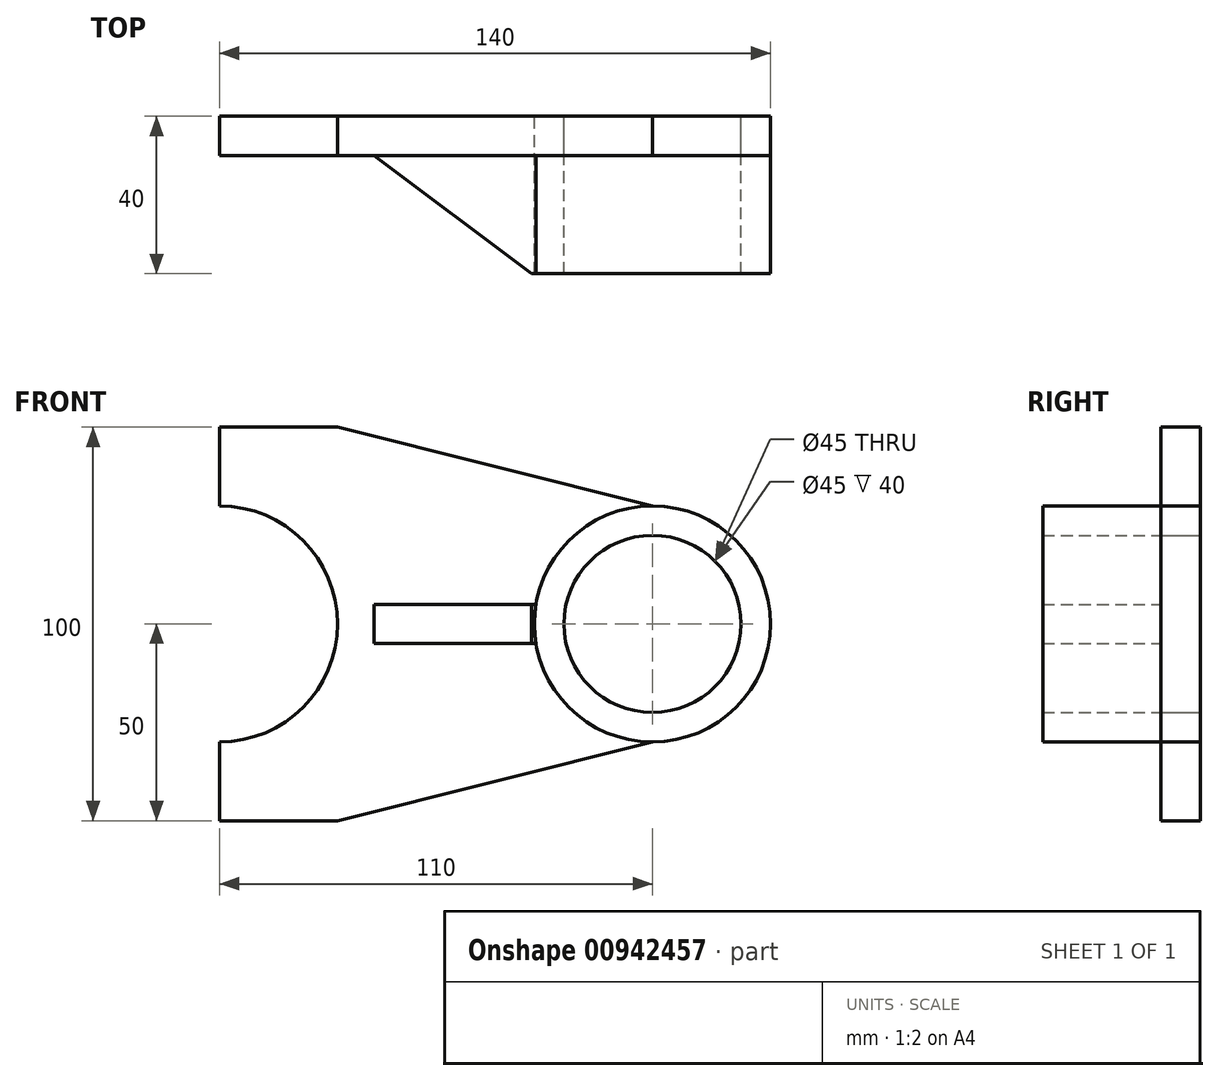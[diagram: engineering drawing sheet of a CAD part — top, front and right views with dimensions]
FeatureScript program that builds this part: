
annotation { "Feature Type Name" : "Feature", "Feature Type Description" : "" }
export const myFeature = defineFeature(function(context is Context, id is Id, definition is map)
    precondition{}
    {
        {
            var Q0;
            Q0=qCreatedBy(makeId("Front.planeOp"),FACE);
            var sketch = newSketch(context, id + "F0", { "sketchPlane" : qUnion([Q0])});
            skCircle(sketch, "E0", {"center": v(0, 0) * mm, "radius": 22.5 * mm});
            skLineSegment(sketch, "E1", {"start": v(-80, 50) * mm, "end": v(-110, 50) * mm});
            skLineSegment(sketch, "E2", {"start": v(-110, 50) * mm, "end": v(-110, 30) * mm});
            skLineSegment(sketch, "E3", {"start": v(-80, -50) * mm, "end": v(-110, -50) * mm});
            skLineSegment(sketch, "E4", {"start": v(-110, -50) * mm, "end": v(-110, -30) * mm});
            skArc(sketch, "E5", {"start": v(-110, -30) * mm, "mid": v(-80, 0) * mm, "end": v(-110, 30) * mm});
            skCircle(sketch, "E6", {"center": v(0, 0) * mm, "radius": 30 * mm});
            skLineSegment(sketch, "E7", {"start": v(-80, 50) * mm, "end": v(0, 30) * mm});
            skLineSegment(sketch, "E8", {"start": v(0, -30) * mm, "end": v(-80, -50) * mm});
            skLineSegment(sketch, "E9", {"start": v(-171.1, 0) * mm, "end": v(99.44, 0) * mm, "construction": true});
            skSolve(sketch);
        }
        {
            var Q0;
            Q0=makeQuery(id+"F0.imprint","IMPRINT",FACE,{"disambiguationData":[TD([[makeQuery(id+"F0.imprint","IMPRINT",EDGE,{"derivedFrom":sQuery(id+"F0.wireOp",EDGE,"E0")}),-1.0]])]});
            extrude(context, id + "F1", {"entities" : qUnion([Q0]), "depth" : 40 * mm, "offsetDistance" : 25 * mm});
        }
        {
            var Q0;
            Q0 = qSketchRegion(id + "F0", true);
            extrude(context, id + "F2", {"entities" : qUnion([Q0]), "depth" : 10 * mm, "offsetDistance" : 25 * mm});
        }
        {
            var Q0;
            Q0=qCreatedBy(makeId("Top.planeOp"),FACE);
            var sketch = newSketch(context, id + "F3", { "sketchPlane" : qUnion([Q0])});
            skLineSegment(sketch, "E10", {"start": v(-30.73, -40) * mm, "end": v(-70.73, -10) * mm});
            skLineSegment(sketch, "E11", {"start": v(-70.73, -10) * mm, "end": v(-28.73, -10) * mm});
            skLineSegment(sketch, "E12", {"start": v(-28.73, -10) * mm, "end": v(-28.73, -40) * mm});
            skLineSegment(sketch, "E13", {"start": v(-28.73, -40) * mm, "end": v(-30.73, -40) * mm});
            skSolve(sketch);
        }
        {
            var Q0;
            Q0=makeQuery(id+"F3.imprint","IMPRINT",FACE,{"disambiguationData":[TD([[makeQuery(id+"F3.imprint","IMPRINT",EDGE,{"derivedFrom":sQuery(id+"F3.wireOp",EDGE,"E10")}),-1.0]])]});
            extrude(context, id + "F4", {"entities" : qUnion([Q0]), "endBound" : BoundingType.SYMMETRIC, "depth" : 10 * mm, "offsetDistance" : 25 * mm});
        }
        {
            var Q0;
            Q0=makeQuery(id+"F1.opExtrude","SWEPT_BODY",BODY,{"disambiguationData":[OSD([sQuery(id+"F0.wireOp",EDGE,"E0"),sQuery(id+"F0.wireOp",EDGE,"E6")])]});
            var Q1;
            Q1=makeQuery(id+"F4.opExtrude","SWEPT_BODY",BODY,{"disambiguationData":[OSD([sQuery(id+"F3.wireOp",EDGE,"E10"),sQuery(id+"F3.wireOp",EDGE,"E11"),sQuery(id+"F3.wireOp",EDGE,"E12"),sQuery(id+"F3.wireOp",EDGE,"E13")])]});
            booleanBodies(context, id + "F5", {"operationType" : BooleanOperationType.SUBTRACTION, "tools" : qUnion([Q0]), "targets" : qUnion([Q1]), "keepTools" : true});
        }
    });
